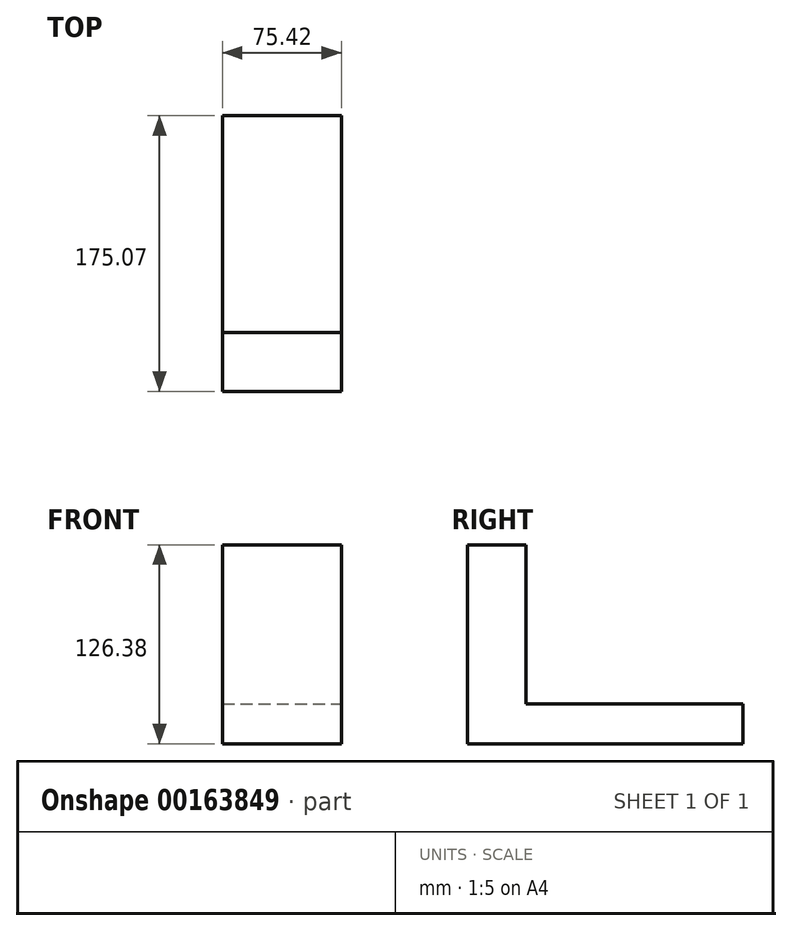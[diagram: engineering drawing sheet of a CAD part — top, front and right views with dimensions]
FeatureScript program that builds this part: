
annotation { "Feature Type Name" : "Feature", "Feature Type Description" : "" }
export const myFeature = defineFeature(function(context is Context, id is Id, definition is map)
    precondition{}
    {
        {
            var Q0;
            Q0=qCreatedBy(makeId("Top.planeOp"),FACE);
            var sketch = newSketch(context, id + "F0", { "sketchPlane" : qUnion([Q0])});
            skLineSegment(sketch, "E0.bottom", {"start": v(0, 0) * mm, "end": v(0, 0) * mm});
            skLineSegment(sketch, "E0.top", {"start": v(0, 0) * mm, "end": v(0, 0) * mm});
            skLineSegment(sketch, "E0.left", {"start": v(0, 0) * mm, "end": v(0, 0) * mm});
            skLineSegment(sketch, "E0.right", {"start": v(0, 0) * mm, "end": v(0, 0) * mm});
            skLineSegment(sketch, "E1.bottom", {"start": v(-21.04, 156.33) * mm, "end": v(54.38, 156.33) * mm});
            skLineSegment(sketch, "E1.top", {"start": v(-21.04, -18.74) * mm, "end": v(54.38, -18.74) * mm});
            skLineSegment(sketch, "E1.left", {"start": v(-21.04, 156.33) * mm, "end": v(-21.04, -18.74) * mm});
            skLineSegment(sketch, "E1.right", {"start": v(54.38, 156.33) * mm, "end": v(54.38, -18.74) * mm});
            skSolve(sketch);
        }
        {
            var Q0;
            Q0=makeQuery(id+"F0.imprint","IMPRINT",FACE,{"disambiguationData":[TD([[makeQuery(id+"F0.imprint","IMPRINT",EDGE,{"derivedFrom":sQuery(id+"F0.wireOp",EDGE,"E1.bottom")}),-1.0]])]});
            var Q1;
            Q1=sQuery(id+"F0.wireOp",EDGE,"E1.top");
            extrude(context, id + "F1", {"entities" : qUnion([Q0]), "surfaceEntities" : qUnion([Q1]), "depth" : 25.4 * mm});
        }
        {
            var Q0;
            Q0=makeQuery(id+"F1.opExtrude","SWEPT_FACE",FACE,{"disambiguationData":[OSD([sQuery(id+"F0.wireOp",EDGE,"E1.top")])]});
            var sketch = newSketch(context, id + "F2", { "sketchPlane" : qUnion([Q0])});
            skLineSegment(sketch, "E2", {"start": v(54.38, 25.4) * mm, "end": v(54.38, 126.38) * mm});
            skLineSegment(sketch, "E3", {"start": v(-21.04, 126.46) * mm, "end": v(-21.04, 25.4) * mm});
            skLineSegment(sketch, "E4", {"start": v(54.38, 126.38) * mm, "end": v(-21.04, 126.38) * mm});
            skSolve(sketch);
        }
        {
            var Q0;
            Q0=makeQuery(id+"F2.imprint","IMPRINT",FACE,{"disambiguationData":[TD([[makeQuery(id+"F2.imprint","IMPRINT",EDGE,{"derivedFrom":sQuery(id+"F2.wireOp",EDGE,"E2")}),1.0]])]});
            extrude(context, id + "F3", {"entities" : qUnion([Q0]), "operationType" : NewBodyOperationType.ADD, "oppositeDirection" : true, "depth" : 37.33 * mm});
        }
    });
